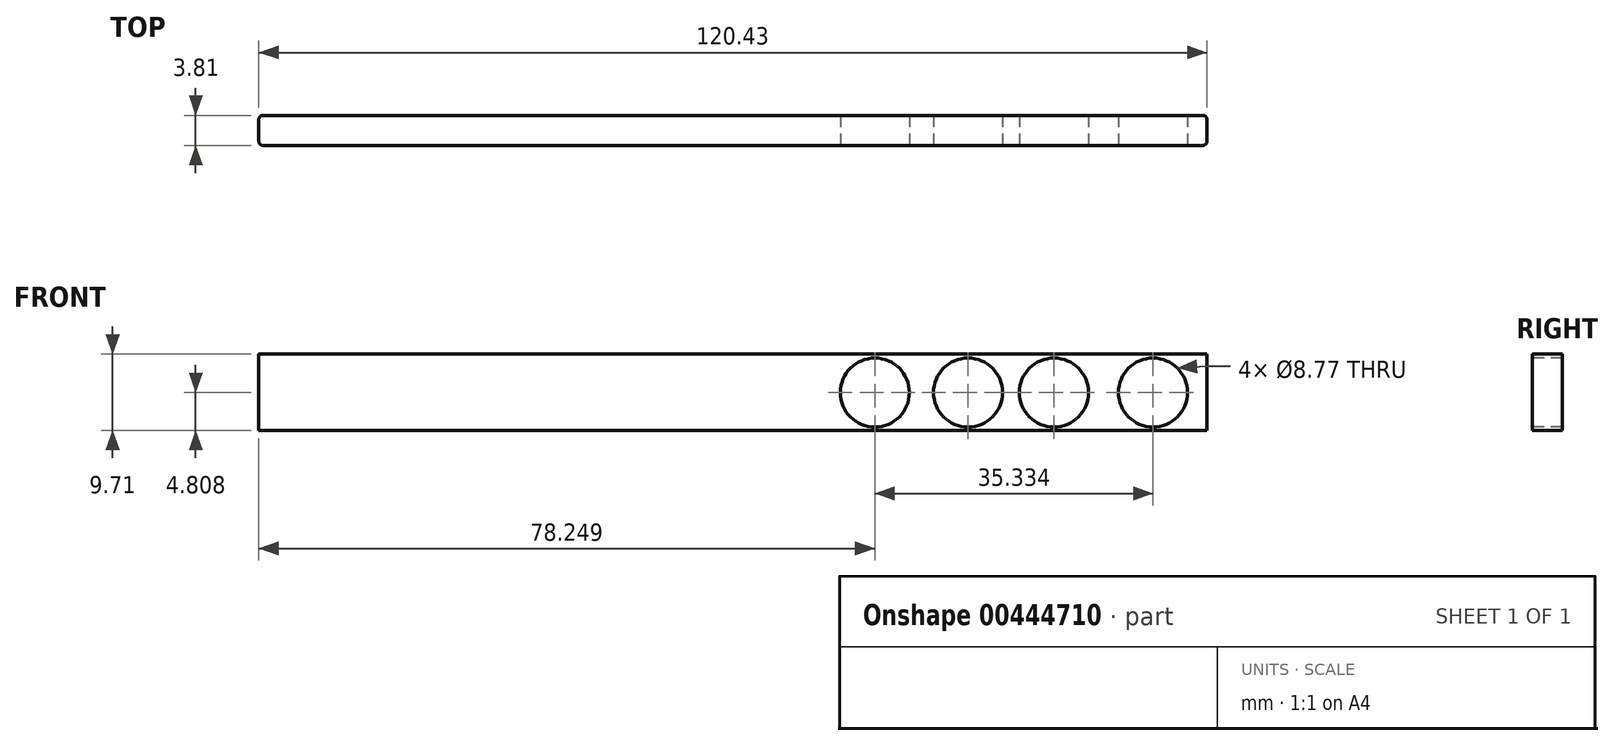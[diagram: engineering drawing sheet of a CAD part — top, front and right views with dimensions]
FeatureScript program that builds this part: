
annotation { "Feature Type Name" : "Feature", "Feature Type Description" : "" }
export const myFeature = defineFeature(function(context is Context, id is Id, definition is map)
    precondition{}
    {
        {
            var Q0;
            Q0=qCreatedBy(makeId("Front.planeOp"),FACE);
            var sketch = newSketch(context, id + "F0", { "sketchPlane" : qUnion([Q0])});
            skLineSegment(sketch, "E0.bottom", {"start": v(-59.38, 0) * mm, "end": v(61.05, 0) * mm});
            skLineSegment(sketch, "E0.top", {"start": v(-59.38, -9.71) * mm, "end": v(61.05, -9.71) * mm});
            skLineSegment(sketch, "E0.left", {"start": v(-59.38, 0) * mm, "end": v(-59.38, -9.71) * mm});
            skLineSegment(sketch, "E0.right", {"start": v(61.05, 0) * mm, "end": v(61.05, -9.71) * mm});
            skSolve(sketch);
        }
        {
            var Q0;
            Q0 = qSketchRegion(id + "F0", true);
            extrude(context, id + "F1", {"entities" : qUnion([Q0]), "depth" : 3.8 * mm});
        }
        {
            var Q0;
            Q0=makeQuery(id+"F1.opExtrude","CAP_FACE",FACE,{"disambiguationData":[OSD([sQuery(id+"F0.wireOp",EDGE,"E0.bottom"),sQuery(id+"F0.wireOp",EDGE,"E0.top"),sQuery(id+"F0.wireOp",EDGE,"E0.left"),sQuery(id+"F0.wireOp",EDGE,"E0.right")])],"isStart":false});
            var sketch = newSketch(context, id + "F2", { "sketchPlane" : qUnion([Q0])});
            skCircle(sketch, "E1", {"center": v(54.2, -4.9) * mm, "radius": 4.39 * mm});
            skCircle(sketch, "E2", {"center": v(41.62, -4.9) * mm, "radius": 4.39 * mm});
            skCircle(sketch, "E3", {"center": v(30.7, -4.9) * mm, "radius": 4.39 * mm});
            skCircle(sketch, "E4", {"center": v(18.87, -4.9) * mm, "radius": 4.39 * mm});
            skSolve(sketch);
        }
        {
            var Q0;
            Q0=makeQuery(id+"F2.imprint","IMPRINT",FACE,{"disambiguationData":[TD([[makeQuery(id+"F2.imprint","IMPRINT",EDGE,{"derivedFrom":sQuery(id+"F2.wireOp",EDGE,"E4")}),1.0]])]});
            var Q1;
            Q1=makeQuery(id+"F2.imprint","IMPRINT",FACE,{"disambiguationData":[TD([[makeQuery(id+"F2.imprint","IMPRINT",EDGE,{"derivedFrom":sQuery(id+"F2.wireOp",EDGE,"E3")}),1.0]])]});
            var Q2;
            Q2=makeQuery(id+"F2.imprint","IMPRINT",FACE,{"disambiguationData":[TD([[makeQuery(id+"F2.imprint","IMPRINT",EDGE,{"derivedFrom":sQuery(id+"F2.wireOp",EDGE,"E2")}),1.0]])]});
            var Q3;
            Q3=makeQuery(id+"F2.imprint","IMPRINT",FACE,{"disambiguationData":[TD([[makeQuery(id+"F2.imprint","IMPRINT",EDGE,{"derivedFrom":sQuery(id+"F2.wireOp",EDGE,"E1")}),1.0]])]});
            var Q4;
            Q4=sQuery(id+"F2.wireOp",EDGE,"E4");
            var Q5;
            Q5=sQuery(id+"F2.wireOp",EDGE,"E3");
            var Q6;
            Q6=sQuery(id+"F2.wireOp",EDGE,"E2");
            var Q7;
            Q7=sQuery(id+"F2.wireOp",EDGE,"E1");
            extrude(context, id + "F3", {"entities" : qUnion([Q0, Q1, Q2, Q3]), "operationType" : NewBodyOperationType.REMOVE, "surfaceEntities" : qUnion([Q4, Q5, Q6, Q7]), "oppositeDirection" : true, "depth" : 38.1 * mm});
        }
        {
            var Q0;
            Q0=makeQuery(id+"F1.opExtrude","CAP_EDGE",EDGE,{"disambiguationData":[OSD([sQuery(id+"F0.wireOp",EDGE,"E0.left")])],"isStart":false});
            var Q1;
            Q1=makeQuery(id+"F1.opExtrude","CAP_EDGE",EDGE,{"disambiguationData":[OSD([sQuery(id+"F0.wireOp",EDGE,"E0.left")])],"isStart":true});
            var Q2;
            Q2=makeQuery(id+"F1.opExtrude","CAP_EDGE",EDGE,{"disambiguationData":[OSD([sQuery(id+"F0.wireOp",EDGE,"E0.right")])],"isStart":true});
            var Q3;
            Q3=makeQuery(id+"F1.opExtrude","CAP_EDGE",EDGE,{"disambiguationData":[OSD([sQuery(id+"F0.wireOp",EDGE,"E0.right")])],"isStart":false});
            fillet(context, id + "F4", {"entities" : qUnion([Q0, Q1, Q2, Q3]), "radius" : 0.5 * mm, "tangentPropagation" : true, "allowEdgeOverflow" : false});
        }
    });
